# Revit family: Panel modular
name_source: partatom
category: Installations électriques
units: mm (PartAtom-declared; Revit-internal decimal feet)

## family parameters
Basée sur le plan de construction = Non
Conserver l'orientation des annotations = Non
Cote de connecteur circulaire = Utiliser le diamètre
Couper avec des vides une fois chargée = Non
Partagée = Non
Point de calcul de pièce = Non
Toujours verticalement = Oui
Type d'élément = Normal

## types (1)
- Panel fibra óptica 1U a equipar
    Adecuado para número de casetes = 4
    Adecuado para número de fibras = 96
    Altura = 44 mm  [stored 0.144357 ft]
    Anchura (mm) = 483 mm
    Clasificación ETIM = EC001130
    Color = IDS_NOIR
    Con carcasa = Oui
    Con conexiones flexibles = Non
    Con placa delantera = Non
    Con portaetiquetas = Oui
    E-catalogo enlace = https://www.legrand.fr
    EAN = 3414970961617
    Elévation par défaut = 0 mm  [stored 0 ft]
    Formulación BIM = Panel fibra óptica 1U a equipar
    Función = Paneles fibra óptica 19 pulgadas a equipar
    IK = IK04
    Numero RAL = 9017
    Número de pieza Legrand = 032100
    Número de unidades de altura = 1
    Profundidad = 334 mm
    Temperatura de almacenamiento = -10°C à 60°C
    Temperatura operativa = -10°C à 60°C
    Tipo de montaje = Montaje de 19 pulgadas

note: [stored X ft] marks values corroborated as IEEE doubles in the binary element streams (Revit-internal decimal feet)
